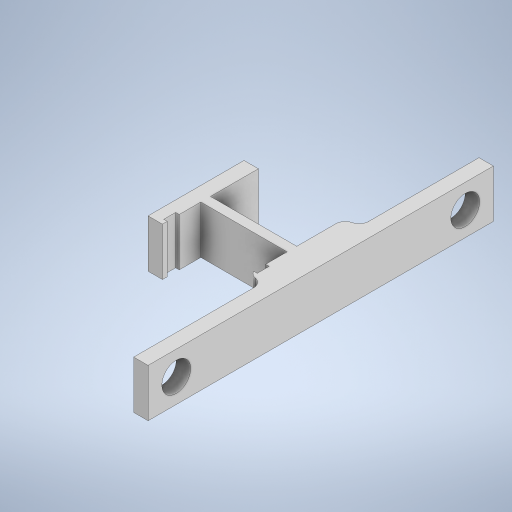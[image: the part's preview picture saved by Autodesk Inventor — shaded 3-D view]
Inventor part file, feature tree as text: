
AUTODESK INVENTOR PART (.ipt)
format: ipt  version: 2024 (Build 280153000, 153)  size: 297,984 bytes
history: native  units: in
note: dims shown in document units (in); Inventor stores cm internally (conversion verified against a paired STEP export)
features: extrude x2, sketch x2, fillet x1
ambient origin geometry x8: Origin, YZ Plane, XZ Plane, XY Plane, X Axis, Y Axis, Z Axis, Center Point
bodies: Solid1 (feature_tree)
feature tree (5):
  extrude  "Extrusion1"  Depth=0.1181in
  fillet  "Fillet1"  Radius=0.1181in
  extrude  "Extrusion2"  Depth=0.3937in
  sketch  "Sketch1"  dims[d0=0.0984in d1=0.1181in d2=0.1181in]
  sketch  "Sketch2"  dims[d3=0.3937in d4=0.3937in d5=0.0787in d6=0.1181in d8=0.0394in d9=0.315in d11=0.0295in d12=0.0295in d13=0.1181in d14=0.3937in d15=0.0in d16=0.7087in d17=0.1181in d18=2.8346in d19=1.378in d20=0.0787in d21=0.2362in d22=0.2362in d23=0.3937in d24=0.1969in d25=0.1969in d26=2.372in d27=2.8346in d28=0.2313in d29=0.0in d30=0.0in]
